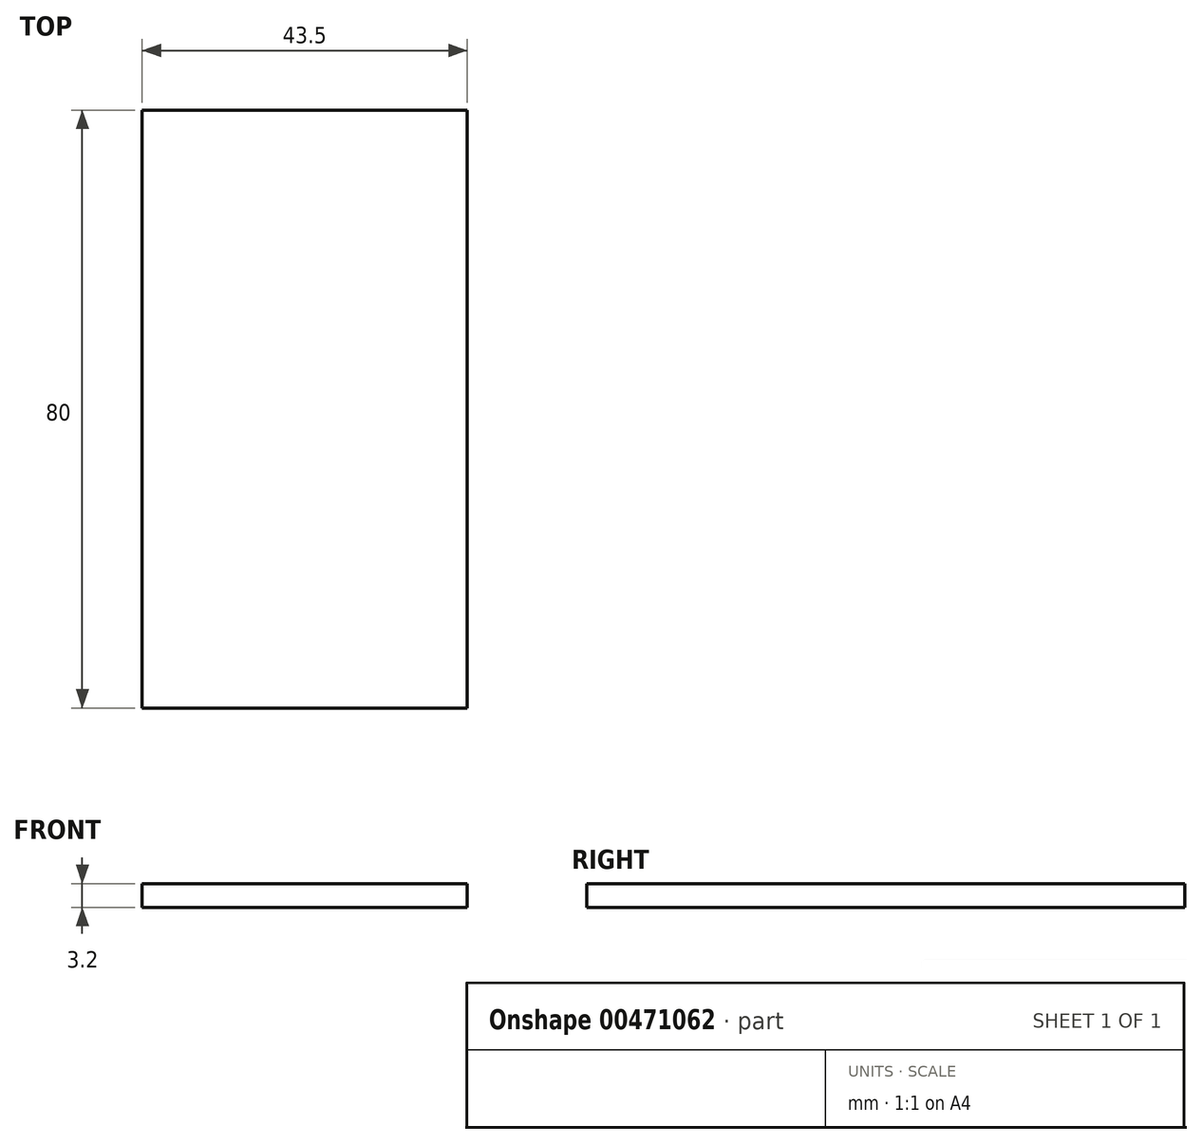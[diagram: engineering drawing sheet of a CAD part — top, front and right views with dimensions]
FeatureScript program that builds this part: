
annotation { "Feature Type Name" : "Feature", "Feature Type Description" : "" }
export const myFeature = defineFeature(function(context is Context, id is Id, definition is map)
    precondition{}
    {
        {
            var Q0;
            Q0=qCreatedBy(makeId("Top.planeOp"),FACE);
            var sketch = newSketch(context, id + "F0", { "sketchPlane" : qUnion([Q0])});
            skLineSegment(sketch, "E0", {"start": v(-75.08, 90.74) * mm, "end": v(-75.08, 10.74) * mm});
            skLineSegment(sketch, "E1", {"start": v(-75.08, 10.74) * mm, "end": v(-31.58, 10.74) * mm});
            skLineSegment(sketch, "E2", {"start": v(-31.58, 10.74) * mm, "end": v(-31.58, 90.74) * mm});
            skLineSegment(sketch, "E3", {"start": v(-31.58, 90.74) * mm, "end": v(-75.08, 90.74) * mm});
            skSolve(sketch);
        }
        {
            var Q0;
            Q0 = qSketchRegion(id + "F0", true);
            extrude(context, id + "F1", {"entities" : qUnion([Q0]), "depth" : 3.2 * mm, "offsetDistance" : 25 * mm});
        }
    });
